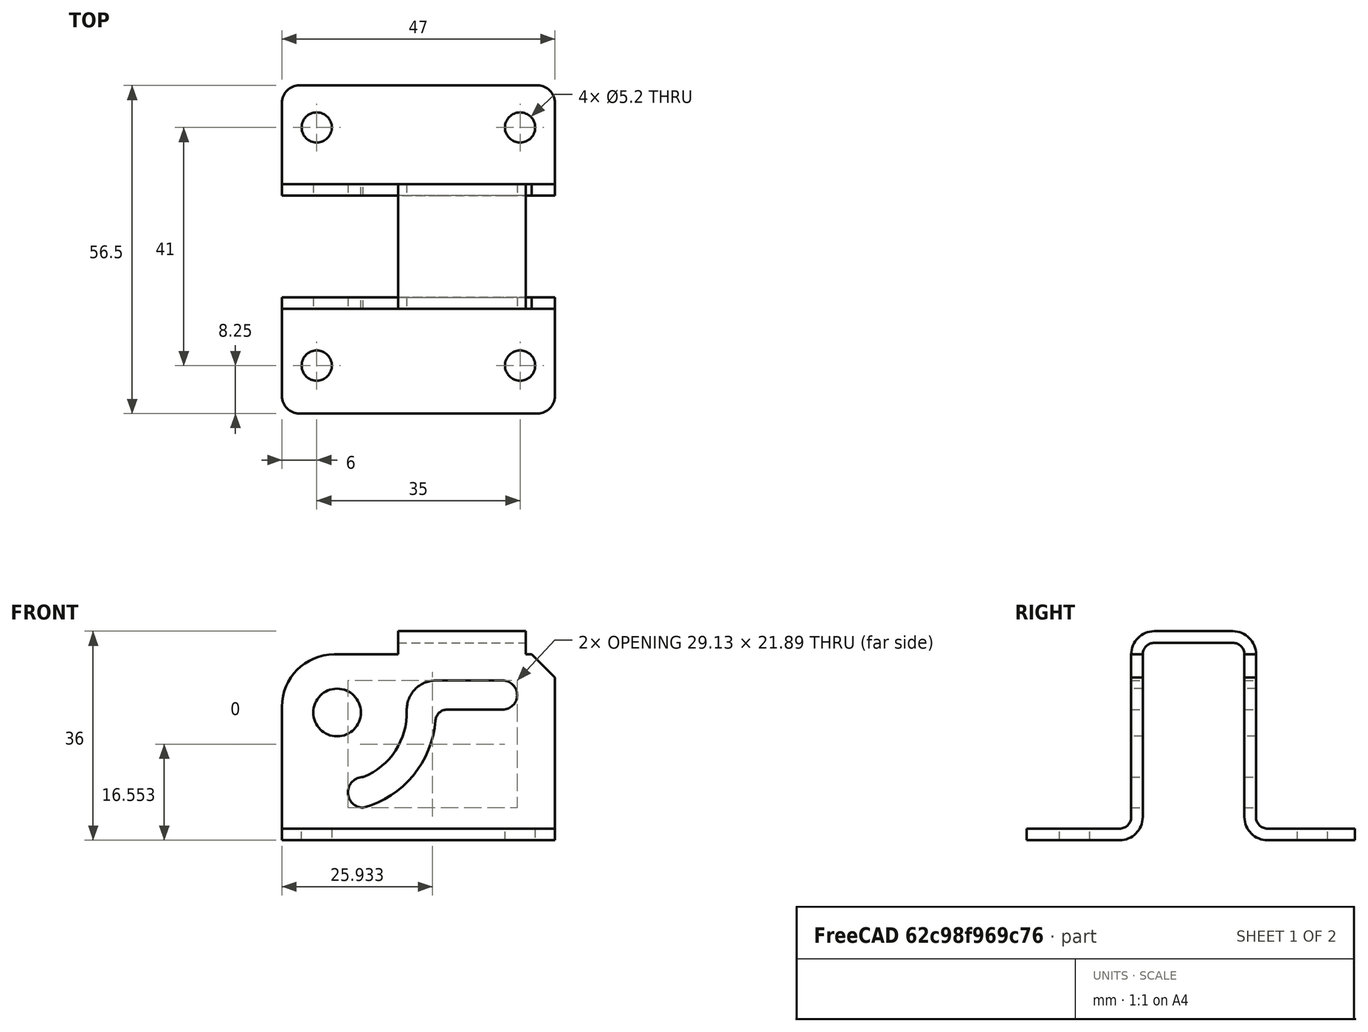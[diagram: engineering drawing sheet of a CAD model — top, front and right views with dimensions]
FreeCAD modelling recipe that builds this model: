
FCSTD DOCUMENT  (FreeCAD 0.21R33668 +26 (Git))
Label: Door Latch Frame
License: All rights reserved
LicenseURL: http://en.wikipedia.org/wiki/All_rights_reserved
objects: TechDraw::DrawViewDimension×9, PartDesign::FeaturePython×8, Sketcher::SketchObject×4, PartDesign::Pocket×3, PartDesign::Fillet×3, TechDraw::DrawProjGroupItem×3, PartDesign::Pad×1, PartDesign::Chamfer×1, PartDesign::Body×1, TechDraw::DrawSVGTemplate×1, TechDraw::DrawViewImage×1, TechDraw::DrawProjGroup×1, TechDraw::DrawPage×1
note: 45 computed .brp shape members not serialized (recipe doc carries the construction recipe); baked Part::Feature solids carry a one-line shape summary decoded from their .brp

FEATURE [Sketcher::SketchObject] Sketch
  FullyConstrained = true
  MapMode = 5
  Support = -> [XY_Plane]
  sketch-geometry (4):
    g0: LineSegment StartX=-11 StartY=6.75 StartZ=0 EndX=11 EndY=6.75 EndZ=0
    g1: LineSegment StartX=11 StartY=6.75 StartZ=0 EndX=11 EndY=-6.75 EndZ=0
    g2: LineSegment StartX=11 StartY=-6.75 StartZ=0 EndX=-11 EndY=-6.75 EndZ=0
    g3: LineSegment StartX=-11 StartY=-6.75 StartZ=0 EndX=-11 EndY=6.75 EndZ=0
  constraints (11):
    c: Coincident(g0,g1)
    c: Coincident(g1,g2)
    c: Coincident(g2,g3)
    c: Coincident(g3,g0)
    c: Horizontal(g0)
    c: Horizontal(g2)
    c: Vertical(g1)
    c: Vertical(g3)
    c: Symmetric(g0,g1,g-1)
    c: DistanceX(g0,g0) = 22
    c: DistanceY(g2,g0) = 13.5
FEATURE [PartDesign::Pad] Pad
  Direction = (0,0,1)
  Length = 2
  Length2 = 10
  Profile = -> Sketch
  ReferenceAxis = -> Sketch [N_Axis]
  Type = 0
FEATURE [PartDesign::FeaturePython] Bend  # WARN: FeaturePython — macro-defined, semantics opaque (R4)
  AutoMiter = true
  BaseFeature = -> Pad
  BendType = 0
  LengthList = [28]
  LengthSpec = 0
  ReliefFactor = 0.7
  UseReliefFactor = false
  angle = 90
  baseObject = -> Pad [Face3]
  bendAList = [90]
  extend1 = 0
  extend2 = 0
  gap1 = 0
  gap2 = 0
  invert = true
  kfactor = 0.5
  length = 28
  maxExtendDist = 5
  minGap = 0.2
  minReliefGap = 1
  miterangle1 = 0
  miterangle2 = 0
  offset = 0
  radius = 2
  reliefType = 0
  reliefd = 1
  reliefw = 0.8
  sketchflip = false
  sketchinvert = false
  unfold = false
FEATURE [PartDesign::FeaturePython] Extend  # WARN: FeaturePython — macro-defined, semantics opaque (R4)
  BaseFeature = -> Bend
  Offset = 0.02
  Refine = true
  UseSubtraction = false
  baseObject = -> Bend [Face1,Face9]
  gap1 = 0
  gap2 = 0
  length = 5
FEATURE [PartDesign::FeaturePython] Extend001  # WARN: FeaturePython — macro-defined, semantics opaque (R4)
  BaseFeature = -> Extend
  Offset = 0.02
  Refine = true
  UseSubtraction = false
  baseObject = -> Extend [Face11]
  gap1 = 0
  gap2 = 0
  length = 15
FEATURE [PartDesign::FeaturePython] Bend001  # WARN: FeaturePython — macro-defined, semantics opaque (R4)
  AutoMiter = true
  BaseFeature = -> Extend001
  BendType = 0
  LengthList = [16]
  LengthSpec = 0
  ReliefFactor = 0.7
  UseReliefFactor = false
  angle = 90
  baseObject = -> Extend001 [Face13]
  bendAList = [90]
  extend1 = 0
  extend2 = 0
  gap1 = 0
  gap2 = 0
  invert = false
  kfactor = 0.5
  length = 16
  maxExtendDist = 5
  minGap = 0.2
  minReliefGap = 1
  miterangle1 = 0
  miterangle2 = 0
  offset = 0
  radius = 2
  reliefType = 0
  reliefd = 1
  reliefw = 0.8
  sketchflip = false
  sketchinvert = false
  unfold = false
FEATURE [PartDesign::FeaturePython] Bend002  # WARN: FeaturePython — macro-defined, semantics opaque (R4)
  AutoMiter = true
  BaseFeature = -> Bend001
  BendType = 0
  LengthList = [28]
  LengthSpec = 0
  ReliefFactor = 0.7
  UseReliefFactor = false
  angle = 90
  baseObject = -> Bend001 [Face22]
  bendAList = [90]
  extend1 = 0
  extend2 = 0
  gap1 = 0
  gap2 = 0
  invert = true
  kfactor = 0.5
  length = 28
  maxExtendDist = 5
  minGap = 0.2
  minReliefGap = 1
  miterangle1 = 0
  miterangle2 = 0
  offset = 0
  radius = 2
  reliefType = 0
  reliefd = 1
  reliefw = 0.8
  sketchflip = false
  sketchinvert = false
  unfold = false
FEATURE [PartDesign::FeaturePython] Extend002  # WARN: FeaturePython — macro-defined, semantics opaque (R4)
  BaseFeature = -> Bend002
  Offset = 0.02
  Refine = true
  UseSubtraction = false
  baseObject = -> Bend002 [Face9,Face1]
  gap1 = 0
  gap2 = 0
  length = 5
FEATURE [PartDesign::FeaturePython] Extend003  # WARN: FeaturePython — macro-defined, semantics opaque (R4)
  BaseFeature = -> Extend002
  Offset = 0.02
  Refine = true
  UseSubtraction = false
  baseObject = -> Extend002 [Face18]
  gap1 = 0
  gap2 = 0
  length = 15
FEATURE [PartDesign::FeaturePython] Bend003  # WARN: FeaturePython — macro-defined, semantics opaque (R4)
  AutoMiter = true
  BaseFeature = -> Extend003
  BendType = 0
  LengthList = [15]
  LengthSpec = 0
  ReliefFactor = 0.7
  UseReliefFactor = false
  angle = 90
  baseObject = -> Extend003 [Face25]
  bendAList = [90]
  extend1 = 0
  extend2 = 0
  gap1 = 0
  gap2 = 0
  invert = false
  kfactor = 0.5
  length = 15
  maxExtendDist = 5
  minGap = 0.2
  minReliefGap = 1
  miterangle1 = 0
  miterangle2 = 0
  offset = 0
  radius = 2
  reliefType = 0
  reliefd = 1
  reliefw = 0.8
  sketchflip = false
  sketchinvert = false
  unfold = false
FEATURE [Sketcher::SketchObject] Sketch001
  FullyConstrained = true
  MapMode = 5
  Placement = pos=(0,0,0) rot=(1,0,0;1.5708rad)
  Support = -> [XZ_Plane]
  sketch-geometry (1):
    g0: Circle CenterX=-21.5 CenterY=-12 CenterZ=0 NormalX=0 NormalY=0 NormalZ=1 AngleXU=0 Radius=4.1
  constraints (3):
    c: Diameter(g0) = 8.2
    c: DistanceX(g0,g-1) = 21.5
    c: DistanceY(g0,g-1) = 12
FEATURE [PartDesign::Pocket] Pocket
  BaseFeature = -> Bend003
  Direction = (0,1,2e-16)
  Length = 26
  Length2 = 5
  Midplane = true
  Profile = -> Sketch001
  ReferenceAxis = -> Sketch001 [N_Axis]
  Type = 0
FEATURE [Sketcher::SketchObject] Sketch002
  FullyConstrained = true
  MapMode = 5
  Support = -> [XY_Plane]
  sketch-geometry (4):
    g0: Circle CenterX=-25 CenterY=20.5 CenterZ=0 NormalX=0 NormalY=0 NormalZ=1 AngleXU=0 Radius=2.6
    g1: Circle CenterX=10 CenterY=20.5 CenterZ=0 NormalX=0 NormalY=0 NormalZ=1 AngleXU=0 Radius=2.6
    g2: Circle CenterX=10 CenterY=-20.5 CenterZ=0 NormalX=0 NormalY=0 NormalZ=1 AngleXU=0 Radius=2.6
    g3: Circle CenterX=-25 CenterY=-20.5 CenterZ=0 NormalX=0 NormalY=0 NormalZ=1 AngleXU=0 Radius=2.6
  constraints (11):
    c: Diameter(g0) = 5.2
    c: Equal(g0,g1)
    c: Equal(g0,g2)
    c: Vertical(g2,g1)
    c: Horizontal(g0,g1)
    c: Horizontal(g3,g2)
    c: Symmetric(g0,g3,g-1)
    c: DistanceX(g0,g1) = 35
    c: DistanceY(g2,g1) = 41
    c: DistanceX(g-1,g1) = 10
    c: Equal(g0,g3)
FEATURE [PartDesign::Pocket] Pocket001
  BaseFeature = -> Pocket
  Direction = (0,0,-1)
  Length = 37
  Length2 = 5
  Profile = -> Sketch002
  ReferenceAxis = -> Sketch002 [N_Axis]
  Type = 0
FEATURE [Sketcher::SketchObject] Sketch003
  FullyConstrained = true
  MapMode = 5
  Placement = pos=(0,0,0) rot=(1,0,0;1.5708rad)
  Support = -> [XZ_Plane]
  sketch-geometry (9):
    g0: GeomPoint X=-21.5 Y=-12 Z=0
    g1: ArcOfCircle CenterX=-21.5 CenterY=-12 CenterZ=0 NormalX=0 NormalY=0 NormalZ=1 AngleXU=0 Radius=12 StartAngle=5.09679 EndAngle=6.31279
    g2: ArcOfCircle CenterX=-21.5 CenterY=-12 CenterZ=0 NormalX=0 NormalY=0 NormalZ=1 AngleXU=0 Radius=17 StartAngle=4.98029 EndAngle=6.3126
    g3: ArcOfCircle CenterX=7 CenterY=-9 CenterZ=0 NormalX=0 NormalY=0 NormalZ=1 AngleXU=0 Radius=2.5 StartAngle=4.71345 EndAngle=7.85398
    g4: LineSegment StartX=7 StartY=-6.5 StartZ=0 EndX=-4.51 EndY=-6.5 EndZ=0
    g5: LineSegment StartX=7.00265 StartY=-11.5 StartZ=0 EndX=-4.50735 EndY=-11.5 EndZ=0
    g6: GeomPoint X=-17 Y=-25.7589 Z=0
    g7: ArcOfCircle CenterX=-17 CenterY=-25.7589 CenterZ=0 NormalX=0 NormalY=0 NormalZ=1 AngleXU=0 Radius=2.63465 StartAngle=1.5708 EndAngle=4.71239
    g8: ArcOfCircle CenterX=-4.50735 CenterY=-11.5 CenterZ=0 NormalX=0 NormalY=0 NormalZ=1 AngleXU=0 Radius=5 StartAngle=1.57133 EndAngle=3.17056
  constraints (25):
    c: DistanceX(g1,g-1) = 17
    c: DistanceX(g0,g-1) = 21.5
    c: DistanceY(g0,g-1) = 12
    c: Coincident(g1,g0)
    c: Coincident(g2,g1)
    c: Radius(g1) = 12
    c: Radius(g2) = 17
    c: Vertical(g2,g1)
    c: Tangent(g3,g4) = -1.5708
    c: DistanceX(g-1,g3) = 7
    c: DistanceY(g3,g-1) = 9
    c: DistanceY(g3,g3) = 5
    c: Horizontal(g4)
    c: Coincident(g5,g3)
    c: Coincident(g5,g2)
    c: Horizontal(g5)
    c: Vertical(g6,g1)
    c: Coincident(g7,g6)
    c: Coincident(g7,g1)
    c: Coincident(g7,g2)
    c: DistanceX(g2,g3) = 11.51
    c: Equal(g5,g4)
    c: Coincident(g8,g2)
    c: Coincident(g8,g4)
    c: Coincident(g8,g1)
FEATURE [PartDesign::Pocket] Pocket002
  BaseFeature = -> Pocket001
  Direction = (0,1,2e-16)
  Length = 31
  Length2 = 5
  Midplane = true
  Profile = -> Sketch003
  ReferenceAxis = -> Sketch003 [N_Axis]
  Type = 0
FEATURE [PartDesign::Fillet] Fillet
  Base = -> Pocket002 [Edge63,Edge130]
  BaseFeature = -> Pocket002
  Radius = 2
  SupportTransform = false
  UseAllEdges = false
FEATURE [PartDesign::Fillet] Fillet001
  Base = -> Fillet [Edge83,Edge40]
  BaseFeature = -> Fillet
  Radius = 9
  SupportTransform = false
  UseAllEdges = false
FEATURE [PartDesign::Fillet] Fillet002
  Base = -> Fillet001 [Edge126,Edge132,Edge88,Edge90]
  BaseFeature = -> Fillet001
  Radius = 3
  SupportTransform = false
  UseAllEdges = false
FEATURE [PartDesign::Chamfer] Chamfer
  Angle = 45
  Base = -> Fillet002 [Edge48,Edge100]
  BaseFeature = -> Fillet002
  ChamferType = 0
  FlipDirection = false
  Size = 4
  Size2 = 1
  SupportTransform = false
  UseAllEdges = false
FEATURE [PartDesign::Body] Body
  Group = -> [Sketch,Pad,Bend,Extend,Extend001,Bend001,Bend002,Extend002,Extend003,Bend003,Sketch001,Pocket,Sketch002,Pocket001,Sketch003,Pocket002,Fillet,Fillet001,Fillet002,Chamfer]
  Origin = -> Origin
  Tip = -> Chamfer
FEATURE [TechDraw::DrawSVGTemplate] Template
  EditableTexts = AUTHOR_NAME=AUTHOR NAME; DN=DN; DRAWING_TITLE=DRAWING TITLE; FC-DATE=DD/MM/YYYY; FC-REV=REV A; FC-SC=SCALE; FC-SH=X / Y; FC-SI=A4; FreeCAD_DRAWING=FreeCAD DRAWING; PN=PN
  Height = 210
  Orientation = 1
  Template = C:/Program Files/FreeCAD 0.21/data/Mod/TechDraw/Templates/A4_Landscape_ISO7200TD.svg
  Width = 297
FEATURE [TechDraw::DrawViewImage] ActiveView
  Height = 100
  ImageFile = <userpath>/AppData/Local/Temp/FreeCAD/Cache/FreeCAD_Doc_c26d5bb2-13bc-4e29-befe-867bf5cd2eb0_b9d391_2140/Pag5B5C.tmp.png
  LockPosition = false
  Rotation = 0
  Scale = 2
  ScaleType = 2
  Width = 100
  X = 74.1454
  Y = 83.2855
FEATURE [TechDraw::DrawProjGroupItem] ProjItem  label="Front"
  CoarseView = false
  Direction = (0,-1,0)
  Focus = 100
  HardHidden = false
  IsoCount = 0
  IsoHidden = false
  IsoVisible = false
  LockPosition = true
  Perspective = false
  Rotation = 0
  RotationVector = (1,0,1e-06)
  Scale = 0.9
  ScaleType = 2
  ScrubCount = 0
  SeamHidden = false
  SeamVisible = false
  SmoothHidden = false
  SmoothVisible = true
  Source = -> [Body]
  Type = 0
  X = 0
  XDirection = (1,0,1e-06)
  Y = 0
FEATURE [TechDraw::DrawProjGroupItem] ProjItem001  label="Top"
  CoarseView = false
  Direction = (-1e-06,0,1)
  Focus = 100
  HardHidden = false
  IsoCount = 0
  IsoHidden = false
  IsoVisible = false
  LockPosition = false
  Perspective = false
  Rotation = 0
  RotationVector = (1,0,0)
  Scale = 0.9
  ScaleType = 2
  ScrubCount = 0
  SeamHidden = false
  SeamVisible = false
  SmoothHidden = false
  SmoothVisible = true
  Source = -> [Body]
  Type = 4
  X = 0
  XDirection = (1,0,1e-06)
  Y = -56.625
FEATURE [TechDraw::DrawProjGroupItem] ProjItem002  label="Right"
  CoarseView = false
  Direction = (1,0,1e-06)
  Focus = 100
  HardHidden = false
  IsoCount = 0
  IsoHidden = false
  IsoVisible = false
  LockPosition = false
  Perspective = false
  Rotation = 0
  RotationVector = (1,0,0)
  Scale = 0.9
  ScaleType = 2
  ScrubCount = 0
  SeamHidden = false
  SeamVisible = false
  SmoothHidden = false
  SmoothVisible = true
  Source = -> [Body]
  Type = 2
  X = -61.575
  XDirection = (0,1,0)
  Y = 0
FEATURE [TechDraw::DrawProjGroup] ProjGroup
  Anchor = -> ProjItem
  AutoDistribute = true
  LockPosition = false
  ProjectionType = 0
  Rotation = 0
  Scale = 0.9
  ScaleType = 2
  Source = -> [Body]
  Views = -> [ProjItem,ProjItem001,ProjItem002]
  X = 220.018
  Y = 161.598
  spacingX = 15
  spacingY = 15
FEATURE [TechDraw::DrawViewDimension] Dimension
  AngleOverride = false
  Arbitrary = false
  ArbitraryTolerances = false
  EqualTolerance = true
  ExtensionAngle = 0
  FormatSpec = %.2w
  FormatSpecOverTolerance = %+.2w
  FormatSpecUnderTolerance = %+.2w
  Inverted = false
  LineAngle = 0
  LockPosition = false
  MeasureType = 1
  OverTolerance = 0
  References2D = -> [ProjItem001]
  Rotation = 0
  Scale = 1.5
  ScaleType = 0
  TheoreticalExact = false
  Type = 2
  UnderTolerance = 0
  X = -32.3226
  Y = 4.0007
FEATURE [TechDraw::DrawViewDimension] Dimension001
  AngleOverride = false
  Arbitrary = false
  ArbitraryTolerances = false
  EqualTolerance = true
  ExtensionAngle = 0
  FormatSpec = %.2w
  FormatSpecOverTolerance = %+.2w
  FormatSpecUnderTolerance = %+.2w
  Inverted = false
  LineAngle = 0
  LockPosition = false
  MeasureType = 1
  OverTolerance = 0
  References2D = -> [ProjItem001]
  Rotation = 0
  Scale = 1.5
  ScaleType = 0
  TheoreticalExact = false
  Type = 1
  UnderTolerance = 0
  X = 2.33999
  Y = 36.8103
FEATURE [TechDraw::DrawViewDimension] Dimension002
  AngleOverride = false
  Arbitrary = false
  ArbitraryTolerances = false
  EqualTolerance = true
  ExtensionAngle = 0
  FormatSpec = %.2w
  FormatSpecOverTolerance = %+.2w
  FormatSpecUnderTolerance = %+.2w
  Inverted = false
  LineAngle = 0
  LockPosition = false
  MeasureType = 1
  OverTolerance = 0
  References2D = -> [ProjItem001]
  Rotation = 0
  Scale = 1.5
  ScaleType = 0
  TheoreticalExact = false
  Type = 1
  UnderTolerance = 0
  X = -9.2812
  Y = 44.8381
FEATURE [TechDraw::DrawViewDimension] Dimension003
  AngleOverride = false
  Arbitrary = false
  ArbitraryTolerances = false
  EqualTolerance = true
  ExtensionAngle = 0
  FormatSpec = %.2w
  FormatSpecOverTolerance = %+.2w
  FormatSpecUnderTolerance = %+.2w
  Inverted = false
  LineAngle = 0
  LockPosition = false
  MeasureType = 1
  OverTolerance = 0
  References2D = -> [ProjItem001]
  Rotation = 0
  Scale = 1.5
  ScaleType = 0
  TheoreticalExact = false
  Type = 2
  UnderTolerance = 0
  X = -42.2659
  Y = 2.5
FEATURE [TechDraw::DrawViewDimension] Dimension004
  AngleOverride = false
  Arbitrary = false
  ArbitraryTolerances = false
  EqualTolerance = true
  ExtensionAngle = 0
  FormatSpec = %.2w
  FormatSpecOverTolerance = %+.2w
  FormatSpecUnderTolerance = %+.2w
  Inverted = false
  LineAngle = 0
  LockPosition = false
  MeasureType = 1
  OverTolerance = 0
  References2D = -> [ProjItem002]
  Rotation = 0
  Scale = 1.5
  ScaleType = 0
  TheoreticalExact = false
  Type = 1
  UnderTolerance = 0
  X = 0.45
  Y = 27.0247
FEATURE [TechDraw::DrawViewDimension] Dimension005
  AngleOverride = false
  Arbitrary = false
  ArbitraryTolerances = false
  EqualTolerance = true
  ExtensionAngle = 0
  FormatSpec = %.2w
  FormatSpecOverTolerance = %+.2w
  FormatSpecUnderTolerance = %+.2w
  Inverted = false
  LineAngle = 0
  LockPosition = false
  MeasureType = 1
  OverTolerance = 0
  References2D = -> [ProjItem002]
  Rotation = 0
  Scale = 1.5
  ScaleType = 0
  TheoreticalExact = false
  Type = 2
  UnderTolerance = 0
  X = 30.3855
  Y = 1.97464
FEATURE [TechDraw::DrawViewDimension] Dimension006
  AngleOverride = false
  Arbitrary = false
  ArbitraryTolerances = false
  EqualTolerance = true
  ExtensionAngle = 0
  FormatSpec = ⌀%.2w
  FormatSpecOverTolerance = %+.2w
  FormatSpecUnderTolerance = %+.2w
  Inverted = false
  LineAngle = 0
  LockPosition = false
  MeasureType = 1
  OverTolerance = 0
  References2D = -> [ProjItem001]
  Rotation = 0
  Scale = 1.5
  ScaleType = 0
  TheoreticalExact = false
  Type = 5
  UnderTolerance = 0
  X = 35.3736
  Y = -8.93095
FEATURE [TechDraw::DrawViewDimension] Dimension007
  AngleOverride = false
  Arbitrary = false
  ArbitraryTolerances = false
  EqualTolerance = true
  ExtensionAngle = 0
  FormatSpec = ⌀%.2w
  FormatSpecOverTolerance = %+.2w
  FormatSpecUnderTolerance = %+.2w
  Inverted = false
  LineAngle = 0
  LockPosition = false
  MeasureType = 1
  OverTolerance = 0
  References2D = -> [ProjItem]
  Rotation = 0
  Scale = 1.5
  ScaleType = 0
  TheoreticalExact = false
  Type = 5
  UnderTolerance = 0
  X = -36.074
  Y = 14.5347
FEATURE [TechDraw::DrawViewDimension] Dimension008
  AngleOverride = false
  Arbitrary = false
  ArbitraryTolerances = false
  EqualTolerance = true
  ExtensionAngle = 0
  FormatSpec = %.2w
  FormatSpecOverTolerance = %+.2w
  FormatSpecUnderTolerance = %+.2w
  Inverted = false
  LineAngle = 0
  LockPosition = false
  MeasureType = 1
  OverTolerance = 0
  References2D = -> [ProjItem]
  Rotation = 0
  Scale = 1.5
  ScaleType = 0
  TheoreticalExact = false
  Type = 2
  UnderTolerance = 0
  X = 37.2173
  Y = -1.00654
FEATURE [TechDraw::DrawPage] Page
  KeepUpdated = true
  NextBalloonIndex = 1
  ProjectionType = 0
  Scale = 1.5
  Template = -> Template
  Views = -> [ActiveView,ProjGroup,Dimension,Dimension001,Dimension002,Dimension003,Dimension004,Dimension005,Dimension006,Dimension007,Dimension008]
